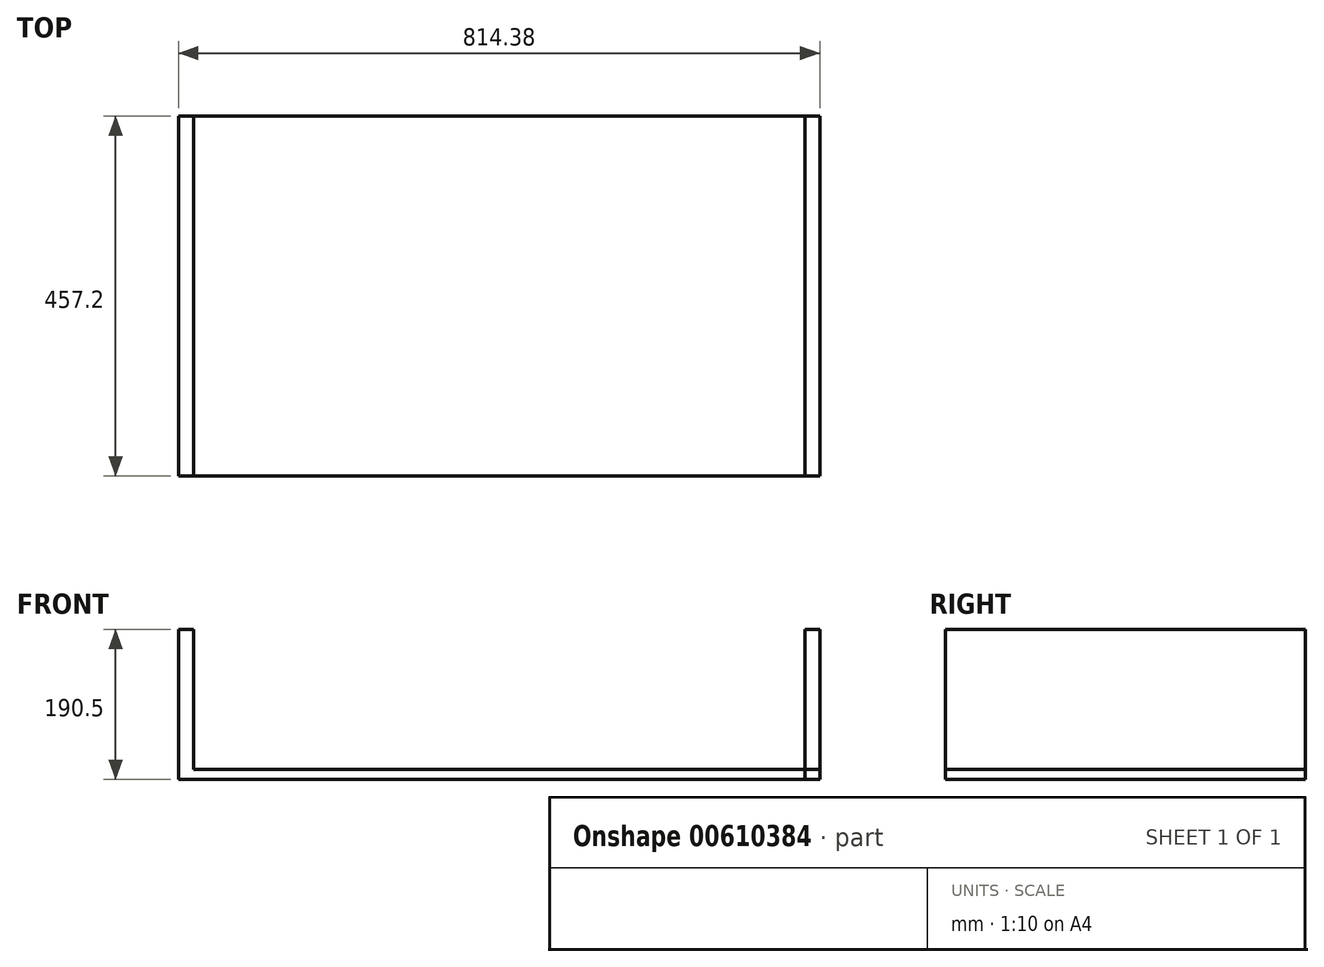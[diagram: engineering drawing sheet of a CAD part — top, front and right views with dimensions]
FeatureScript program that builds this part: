
annotation { "Feature Type Name" : "Feature", "Feature Type Description" : "" }
export const myFeature = defineFeature(function(context is Context, id is Id, definition is map)
    precondition{}
    {
        {
            var Q0;
            Q0=qCreatedBy(makeId("Top.planeOp"),FACE);
            var sketch = newSketch(context, id + "F0", { "sketchPlane" : qUnion([Q0])});
            skLineSegment(sketch, "E0.bottom", {"start": v(388.14, -228.6) * mm, "end": v(-388.14, -228.6) * mm});
            skLineSegment(sketch, "E0.top", {"start": v(388.14, 228.6) * mm, "end": v(-388.14, 228.6) * mm});
            skLineSegment(sketch, "E0.left", {"start": v(388.14, -228.6) * mm, "end": v(388.14, 228.6) * mm});
            skLineSegment(sketch, "E0.right", {"start": v(-388.14, -228.6) * mm, "end": v(-388.14, 228.6) * mm});
            skPoint(sketch, "E0.middle", {"position": v(0, 0) * mm});
            skSolve(sketch);
        }
        {
            var Q0;
            Q0=makeQuery(id+"F0.imprint","IMPRINT",FACE,{"disambiguationData":[TD([[makeQuery(id+"F0.imprint","IMPRINT",EDGE,{"derivedFrom":sQuery(id+"F0.wireOp",EDGE,"E0.bottom")}),-1.0]])]});
            extrude(context, id + "F1", {"entities" : qUnion([Q0]), "depth" : 12.7 * mm, "offsetDistance" : 25.4 * mm});
        }
        {
            var Q0;
            Q0=makeQuery(id+"F1.opExtrude","SWEPT_FACE",FACE,{"disambiguationData":[OSD([sQuery(id+"F0.wireOp",EDGE,"E0.left")])]});
            var sketch = newSketch(context, id + "F2", { "sketchPlane" : qUnion([Q0])});
            skLineSegment(sketch, "E1.bottom", {"start": v(-228.6, 0) * mm, "end": v(228.6, 0) * mm});
            skLineSegment(sketch, "E1.top", {"start": v(-228.6, 190.5) * mm, "end": v(228.6, 190.5) * mm});
            skLineSegment(sketch, "E1.left", {"start": v(-228.6, 0) * mm, "end": v(-228.6, 190.5) * mm});
            skLineSegment(sketch, "E1.right", {"start": v(228.6, 0) * mm, "end": v(228.6, 190.5) * mm});
            skSolve(sketch);
        }
        {
            var Q0;
            {var subQ0=sQuery(id+"F2.wireOp",EDGE,"E1.top");Q0=makeQuery(id+"F2.imprint","IMPRINT",FACE,{"disambiguationData":[TD([[makeQuery(id+"F2.imprint","IMPRINT",EDGE,{"derivedFrom":subQ0}),-1.0]])]});}
            extrude(context, id + "F3", {"entities" : qUnion([Q0]), "depth" : 19.05 * mm, "offsetDistance" : 25.4 * mm});
        }
        {
            var Q0;
            Q0=makeQuery(id+"F3.opExtrude","SWEPT_FACE",FACE,{"disambiguationData":[OSD([sQuery(id+"F0.wireOp",EDGE,"E0.left")])]});
            extrude(context, id + "F4", {"entities" : qUnion([Q0]), "depth" : 12.7 * mm, "offsetDistance" : 25.4 * mm});
        }
        {
            var Q0;
            Q0=makeQuery(id+"F1.opExtrude","SWEPT_FACE",FACE,{"disambiguationData":[OSD([sQuery(id+"F0.wireOp",EDGE,"E0.right")])]});
            var sketch = newSketch(context, id + "F5", { "sketchPlane" : qUnion([Q0])});
            skLineSegment(sketch, "E2.bottom", {"start": v(228.6, 0) * mm, "end": v(-228.6, 0) * mm});
            skLineSegment(sketch, "E2.top", {"start": v(228.6, 190.5) * mm, "end": v(-228.6, 190.5) * mm});
            skLineSegment(sketch, "E2.left", {"start": v(228.6, 0) * mm, "end": v(228.6, 190.5) * mm});
            skLineSegment(sketch, "E2.right", {"start": v(-228.6, 0) * mm, "end": v(-228.6, 190.5) * mm});
            skSolve(sketch);
        }
        {
            var Q0;
            Q0 = qSketchRegion(id + "F5", true);
            extrude(context, id + "F6", {"entities" : qUnion([Q0]), "operationType" : NewBodyOperationType.ADD, "depth" : 19.05 * mm, "offsetDistance" : 25.4 * mm});
        }
    });
